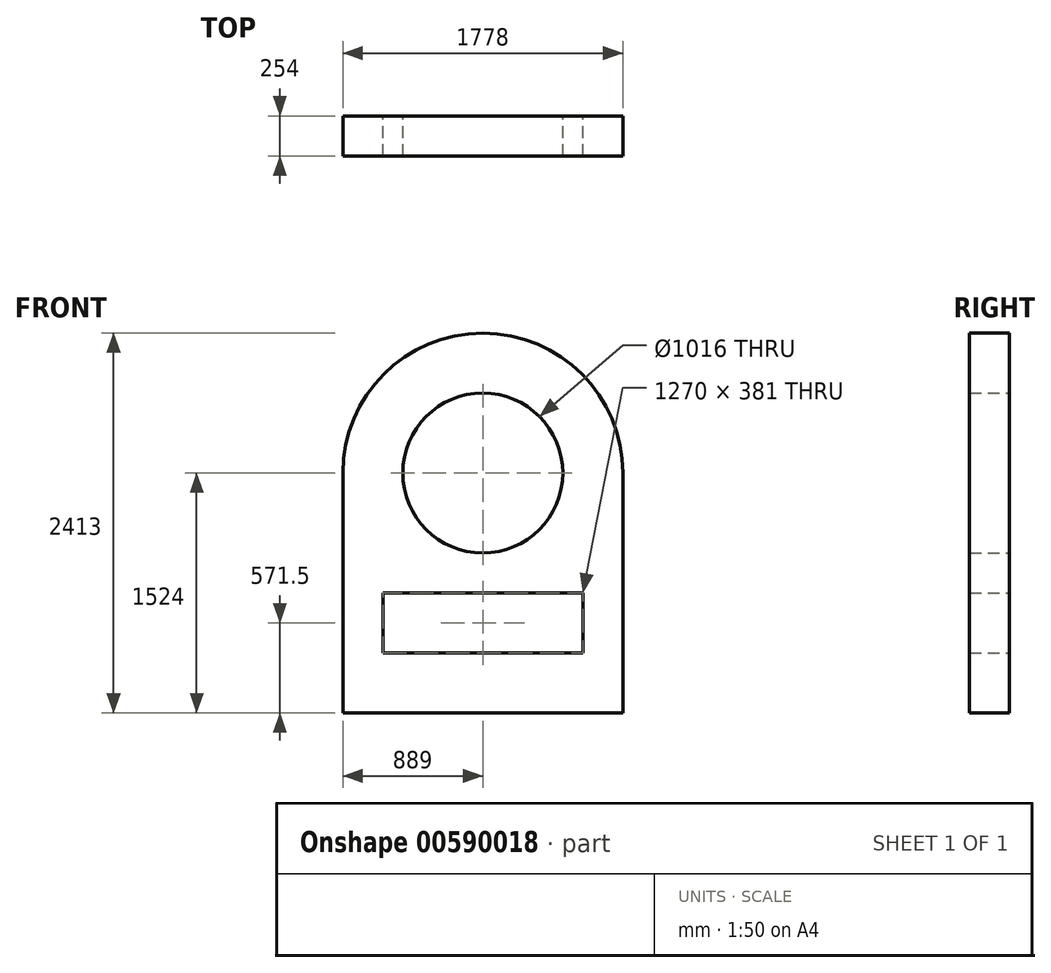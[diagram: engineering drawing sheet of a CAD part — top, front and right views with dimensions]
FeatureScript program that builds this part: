
annotation { "Feature Type Name" : "Feature", "Feature Type Description" : "" }
export const myFeature = defineFeature(function(context is Context, id is Id, definition is map)
    precondition{}
    {
        {
            var Q0;
            Q0=qCreatedBy(makeId("Front.planeOp"),FACE);
            var sketch = newSketch(context, id + "F0", { "sketchPlane" : qUnion([Q0])});
            skLineSegment(sketch, "E0", {"start": v(0, 0) * mm, "end": v(-1778, 0) * mm});
            skLineSegment(sketch, "E1", {"start": v(-1778, 0) * mm, "end": v(-1778, 1524) * mm});
            skPoint(sketch, "E2.endSnap0", {"position": v(-1778, 762) * mm});
            skLineSegment(sketch, "E3", {"start": v(-1524, 381) * mm, "end": v(-254, 381) * mm});
            skLineSegment(sketch, "E4", {"start": v(-254, 381) * mm, "end": v(-254, 762) * mm});
            skLineSegment(sketch, "E5", {"start": v(-254, 762) * mm, "end": v(-1524, 762) * mm});
            skLineSegment(sketch, "E6", {"start": v(-1524, 762) * mm, "end": v(-1524, 381) * mm});
            skLineSegment(sketch, "E7", {"start": v(0, 0) * mm, "end": v(0, 1524) * mm});
            skCircle(sketch, "E8", {"center": v(-889, 1524) * mm, "radius": 508 * mm});
            skArc(sketch, "E9", {"start": v(0, 1524) * mm, "mid": v(-889, 2413) * mm, "end": v(-1778, 1524) * mm});
            skSolve(sketch);
        }
        {
            var Q0;
            Q0=makeQuery(id+"F0.imprint","IMPRINT",FACE,{"disambiguationData":[TD([[makeQuery(id+"F0.imprint","IMPRINT",EDGE,{"derivedFrom":sQuery(id+"F0.wireOp",EDGE,"E0")}),-1.0]])]});
            extrude(context, id + "F1", {"entities" : qUnion([Q0]), "depth" : 254 * mm, "offsetDistance" : 25.4 * mm});
        }
    });
